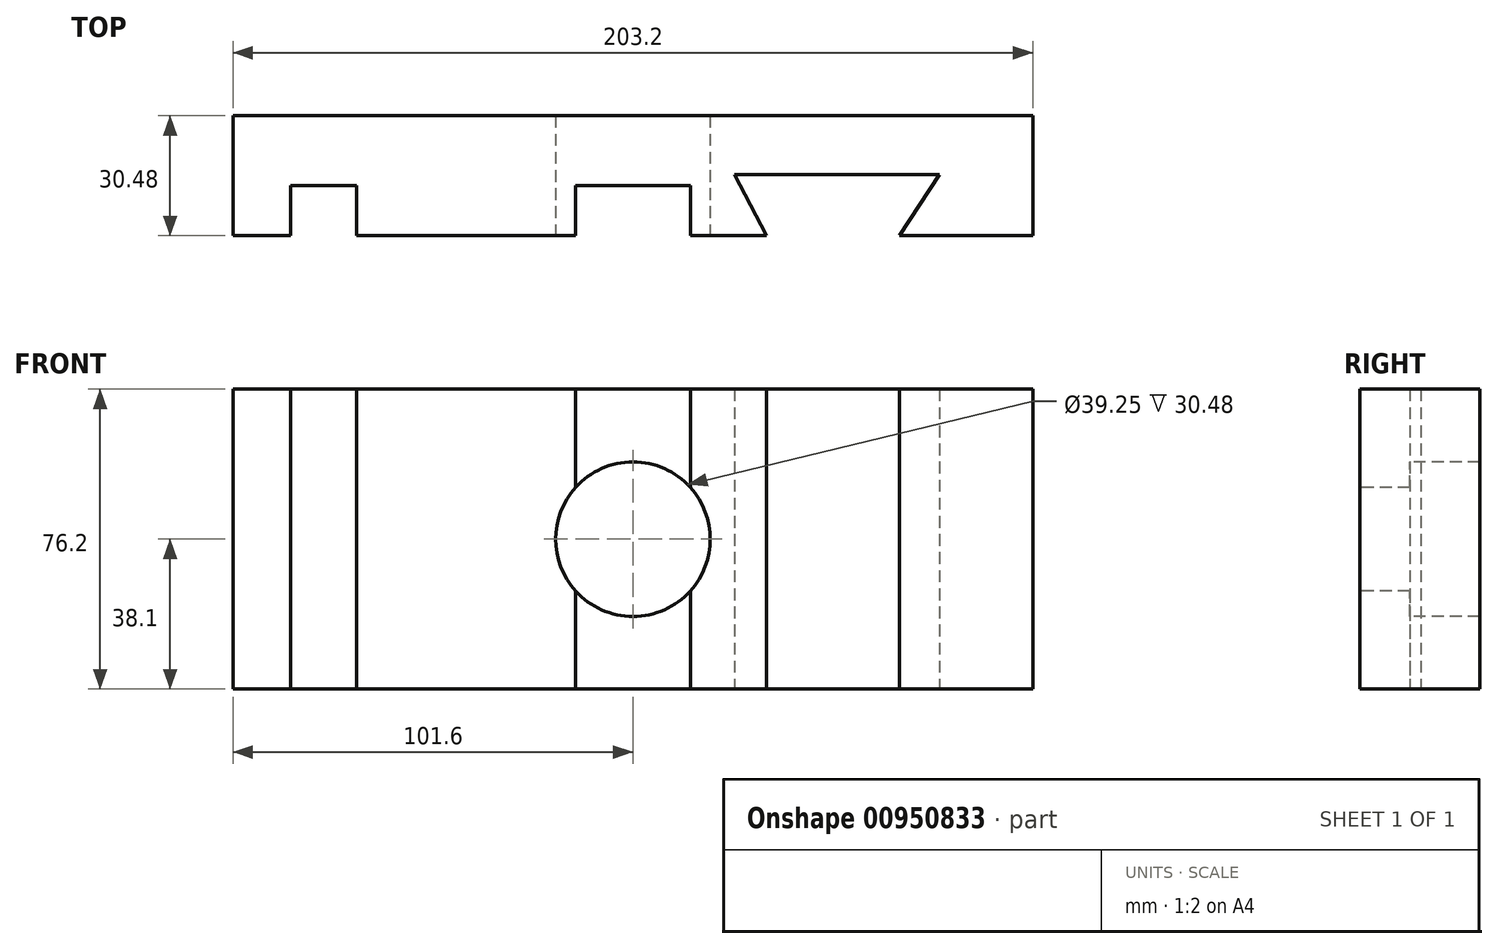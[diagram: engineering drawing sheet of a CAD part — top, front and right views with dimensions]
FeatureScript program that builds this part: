
annotation { "Feature Type Name" : "Feature", "Feature Type Description" : "" }
export const myFeature = defineFeature(function(context is Context, id is Id, definition is map)
    precondition{}
    {
        {
            var Q0;
            Q0=qCreatedBy(makeId("Front.planeOp"),FACE);
            var sketch = newSketch(context, id + "F0", { "sketchPlane" : qUnion([Q0])});
            skLineSegment(sketch, "E0.bottom", {"start": v(-101.6, 38.1) * mm, "end": v(101.6, 38.1) * mm});
            skLineSegment(sketch, "E0.top", {"start": v(-101.6, -38.1) * mm, "end": v(101.6, -38.1) * mm});
            skLineSegment(sketch, "E0.left", {"start": v(-101.6, 38.1) * mm, "end": v(-101.6, -38.1) * mm});
            skLineSegment(sketch, "E0.right", {"start": v(101.6, 38.1) * mm, "end": v(101.6, -38.1) * mm});
            skPoint(sketch, "E0.middle", {"position": v(0, 0) * mm});
            skSolve(sketch);
        }
        {
            var Q0;
            Q0=makeQuery(id+"F0.imprint","IMPRINT",FACE,{"disambiguationData":[TD([[makeQuery(id+"F0.imprint","IMPRINT",EDGE,{"derivedFrom":sQuery(id+"F0.wireOp",EDGE,"E0.bottom")}),-1.0]])]});
            extrude(context, id + "F1", {"entities" : qUnion([Q0]), "depth" : 30.48 * mm, "offsetDistance" : 25.4 * mm});
        }
        {
            var Q0;
            Q0=makeQuery(id+"F1.opExtrude","CAP_FACE",FACE,{"disambiguationData":[OSD([sQuery(id+"F0.wireOp",EDGE,"E0.bottom"),sQuery(id+"F0.wireOp",EDGE,"E0.top"),sQuery(id+"F0.wireOp",EDGE,"E0.left"),sQuery(id+"F0.wireOp",EDGE,"E0.right")])],"isStart":false});
            var sketch = newSketch(context, id + "F2", { "sketchPlane" : qUnion([Q0])});
            skCircle(sketch, "E1", {"center": v(0, 0) * mm, "radius": 19.63 * mm});
            skSolve(sketch);
        }
        {
            var Q0;
            Q0=makeQuery(id+"F2.imprint","IMPRINT",FACE,{"disambiguationData":[TD([[makeQuery(id+"F2.imprint","IMPRINT",EDGE,{"derivedFrom":sQuery(id+"F2.wireOp",EDGE,"E1")}),1.0]])]});
            extrude(context, id + "F3", {"entities" : qUnion([Q0]), "operationType" : NewBodyOperationType.REMOVE, "endBound" : BoundingType.THROUGH_ALL, "oppositeDirection" : true, "depth" : 25.4 * mm, "offsetDistance" : 25.4 * mm});
        }
        {
            var Q0;
            Q0=makeQuery(id+"F1.opExtrude","CAP_FACE",FACE,{"disambiguationData":[OSD([sQuery(id+"F0.wireOp",EDGE,"E0.bottom"),sQuery(id+"F0.wireOp",EDGE,"E0.top"),sQuery(id+"F0.wireOp",EDGE,"E0.left"),sQuery(id+"F0.wireOp",EDGE,"E0.right")])],"isStart":false});
            var sketch = newSketch(context, id + "F4", { "sketchPlane" : qUnion([Q0])});
            skLineSegment(sketch, "E2.bottom", {"start": v(-86.98, 38.1) * mm, "end": v(-70.17, 38.1) * mm});
            skLineSegment(sketch, "E2.top", {"start": v(-86.98, -38.1) * mm, "end": v(-70.17, -38.1) * mm});
            skLineSegment(sketch, "E2.left", {"start": v(-86.98, 38.1) * mm, "end": v(-86.98, -38.1) * mm});
            skLineSegment(sketch, "E2.right", {"start": v(-70.17, 38.1) * mm, "end": v(-70.17, -38.1) * mm});
            skLineSegment(sketch, "E3", {"start": v(-14.56, 38.1) * mm, "end": v(-14.56, -38.1) * mm});
            skLineSegment(sketch, "E4", {"start": v(-14.56, -38.1) * mm, "end": v(14.56, -38.1) * mm});
            skLineSegment(sketch, "E5", {"start": v(14.56, -38.1) * mm, "end": v(14.56, 38.1) * mm});
            skLineSegment(sketch, "E6", {"start": v(14.56, 38.1) * mm, "end": v(-14.56, 38.1) * mm});
            skLineSegment(sketch, "E7", {"start": v(0, 38.1) * mm, "end": v(0, -38.1) * mm, "construction": true});
            skSolve(sketch);
        }
        {
            var Q0;
            Q0=makeQuery(id+"F4.imprint","IMPRINT",FACE,{"disambiguationData":[TD([[makeQuery(id+"F4.imprint","IMPRINT",EDGE,{"derivedFrom":sQuery(id+"F4.wireOp",EDGE,"E2.bottom")}),-1.0]])]});
            var Q1;
            {var subQ0=sQuery(id+"F4.wireOp",EDGE,"E4");Q1=makeQuery(id+"F4.imprint","IMPRINT",FACE,{"disambiguationData":[TD([[makeQuery(id+"F4.imprint","IMPRINT",EDGE,{"derivedFrom":subQ0}),1.0]])]});}
            var Q2;
            {var subQ0=sQuery(id+"F4.wireOp",EDGE,"E6");Q2=makeQuery(id+"F4.imprint","IMPRINT",FACE,{"disambiguationData":[TD([[makeQuery(id+"F4.imprint","IMPRINT",EDGE,{"derivedFrom":subQ0}),-1.0]])]});}
            extrude(context, id + "F5", {"entities" : qUnion([Q0, Q1, Q2]), "operationType" : NewBodyOperationType.REMOVE, "oppositeDirection" : true, "depth" : 12.7 * mm, "offsetDistance" : 25.4 * mm});
        }
        {
            var Q0;
            Q0=makeQuery(id+"F1.opExtrude","SWEPT_FACE",FACE,{"disambiguationData":[OSD([sQuery(id+"F0.wireOp",EDGE,"E0.top")])]});
            var sketch = newSketch(context, id + "F6", { "sketchPlane" : qUnion([Q0])});
            skLineSegment(sketch, "E8", {"start": v(33.9, 30.48) * mm, "end": v(25.85, 15) * mm});
            skLineSegment(sketch, "E9", {"start": v(25.85, 15) * mm, "end": v(77.9, 15) * mm});
            skLineSegment(sketch, "E10", {"start": v(77.9, 15) * mm, "end": v(67.77, 30.48) * mm});
            skLineSegment(sketch, "E11", {"start": v(67.77, 30.48) * mm, "end": v(33.9, 30.48) * mm});
            skSolve(sketch);
        }
        {
            var Q0;
            Q0=makeQuery(id+"F6.imprint","IMPRINT",FACE,{"disambiguationData":[TD([[makeQuery(id+"F6.imprint","IMPRINT",EDGE,{"derivedFrom":sQuery(id+"F6.wireOp",EDGE,"E8")}),1.0]])]});
            extrude(context, id + "F7", {"entities" : qUnion([Q0]), "operationType" : NewBodyOperationType.REMOVE, "endBound" : BoundingType.THROUGH_ALL, "oppositeDirection" : true, "depth" : 25.4 * mm, "offsetDistance" : 25.4 * mm});
        }
    });
